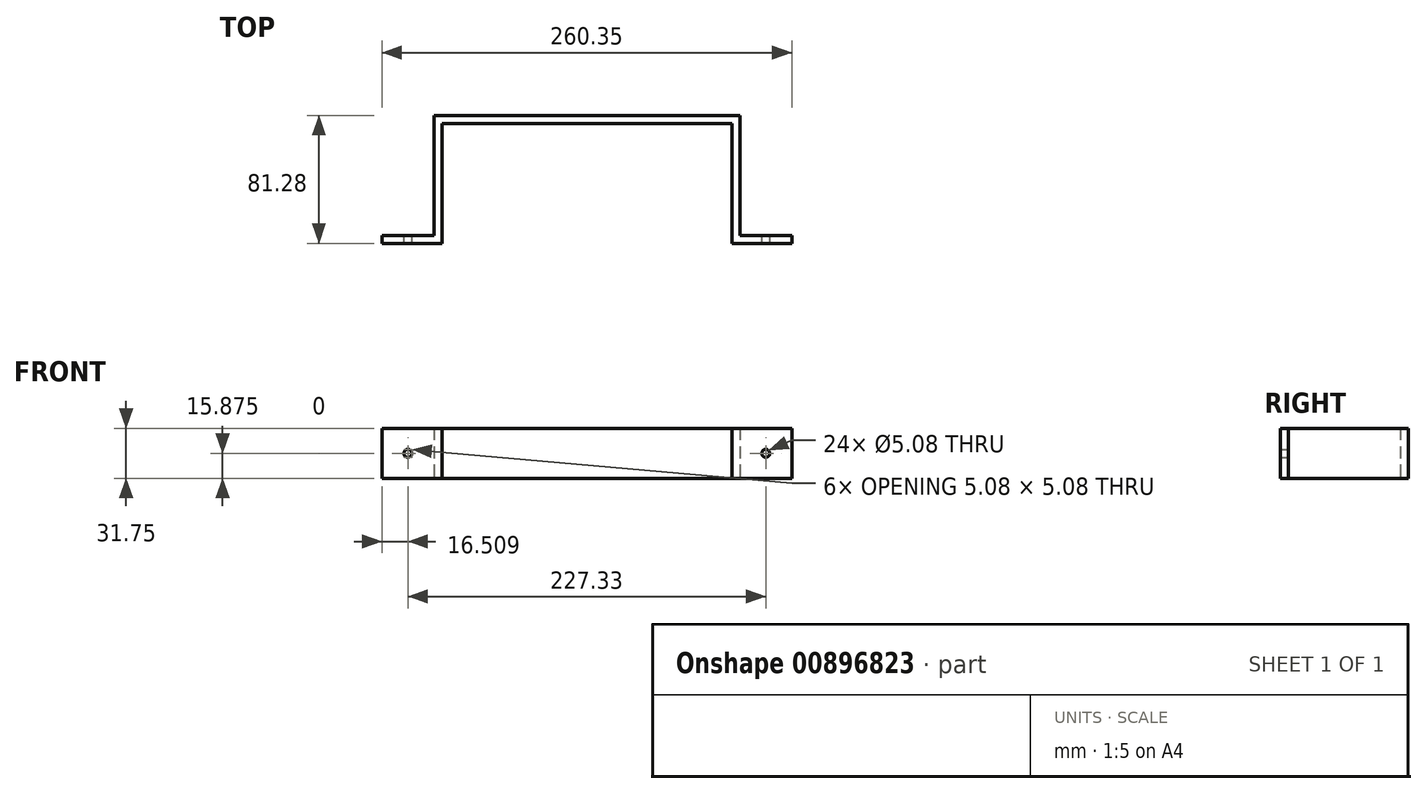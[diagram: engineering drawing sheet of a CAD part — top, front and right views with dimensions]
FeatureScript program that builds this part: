
annotation { "Feature Type Name" : "Feature", "Feature Type Description" : "" }
export const myFeature = defineFeature(function(context is Context, id is Id, definition is map)
    precondition{}
    {
        {
            var Q0;
            Q0=qCreatedBy(makeId("Top.planeOp"),FACE);
            var sketch = newSketch(context, id + "F0", { "sketchPlane" : qUnion([Q0])});
            skLineSegment(sketch, "E0", {"start": v(-81.06, 47.3) * mm, "end": v(103.09, 47.3) * mm});
            skLineSegment(sketch, "E1", {"start": v(103.09, 47.3) * mm, "end": v(103.09, -28.9) * mm});
            skLineSegment(sketch, "E2", {"start": v(-81.06, 47.3) * mm, "end": v(-81.06, -28.9) * mm});
            skLineSegment(sketch, "E3", {"start": v(-81.06, -28.9) * mm, "end": v(-119.16, -28.9) * mm});
            skLineSegment(sketch, "E4", {"start": v(103.09, -28.9) * mm, "end": v(141.19, -28.9) * mm});
            skLineSegment(sketch, "E5", {"start": v(-119.16, -28.9) * mm, "end": v(-119.16, -23.82) * mm});
            skLineSegment(sketch, "E6", {"start": v(-119.16, -23.82) * mm, "end": v(-86.14, -23.82) * mm});
            skLineSegment(sketch, "E7", {"start": v(-86.14, -23.82) * mm, "end": v(-86.14, 52.38) * mm});
            skLineSegment(sketch, "E8", {"start": v(-86.14, 52.38) * mm, "end": v(108.17, 52.38) * mm});
            skLineSegment(sketch, "E9", {"start": v(141.19, -28.9) * mm, "end": v(141.19, -23.82) * mm});
            skLineSegment(sketch, "E10", {"start": v(141.19, -23.82) * mm, "end": v(108.17, -23.82) * mm});
            skLineSegment(sketch, "E11", {"start": v(108.17, -23.82) * mm, "end": v(108.17, 52.38) * mm});
            skSolve(sketch);
        }
        {
            var Q0;
            Q0=makeQuery(id+"F0.imprint","IMPRINT",FACE,{"disambiguationData":[TD([[makeQuery(id+"F0.imprint","IMPRINT",EDGE,{"derivedFrom":sQuery(id+"F0.wireOp",EDGE,"E0")}),1.0]])]});
            extrude(context, id + "F1", {"entities" : qUnion([Q0]), "depth" : 31.75 * mm, "offsetDistance" : 25.4 * mm});
        }
        {
            var Q0;
            Q0=makeQuery(id+"F1.opExtrude","SWEPT_FACE",FACE,{"disambiguationData":[OSD([sQuery(id+"F0.wireOp",EDGE,"E6")])]});
            var sketch = newSketch(context, id + "F2", { "sketchPlane" : qUnion([Q0])});
            skCircle(sketch, "E12", {"center": v(102.65, 15.88) * mm, "radius": 3.18 * mm});
            skSolve(sketch);
        }
        {
            var Q0;
            Q0=sQuery(id+"F2.wireOp",VERTEX,"E12.center");
            var Q1;
            Q1=makeQuery(id+"F1.opExtrude","SWEPT_BODY",BODY,{"disambiguationData":[OSD([sQuery(id+"F0.wireOp",EDGE,"E0"),sQuery(id+"F0.wireOp",EDGE,"E1"),sQuery(id+"F0.wireOp",EDGE,"E2"),sQuery(id+"F0.wireOp",EDGE,"E3"),sQuery(id+"F0.wireOp",EDGE,"E4"),sQuery(id+"F0.wireOp",EDGE,"E5"),sQuery(id+"F0.wireOp",EDGE,"E6"),sQuery(id+"F0.wireOp",EDGE,"E7"),sQuery(id+"F0.wireOp",EDGE,"E8"),sQuery(id+"F0.wireOp",EDGE,"E9"),sQuery(id+"F0.wireOp",EDGE,"E10"),sQuery(id+"F0.wireOp",EDGE,"E11")])]});
            hole(context, id + "F3", {"style" : HoleStyle.SIMPLE, "endStyle" : HoleEndStyle.THROUGH, "holeDiameter" : 5.08 * mm, "majorDiameter" : 6.35 * mm, "isTappedThrough" : true, "tappedDepth" : 12.7 * mm, "tapClearance" : 3, "locations" : qUnion([Q0]), "scope" : qUnion([Q1])});
        }
        {
            var Q0;
            Q0=makeQuery(id+"F1.opExtrude","SWEPT_FACE",FACE,{"disambiguationData":[OSD([sQuery(id+"F0.wireOp",EDGE,"E10")])]});
            var sketch = newSketch(context, id + "F4", { "sketchPlane" : qUnion([Q0])});
            skCircle(sketch, "E13", {"center": v(-124.68, 15.88) * mm, "radius": 3.18 * mm});
            skSolve(sketch);
        }
        {
            var Q0;
            Q0=sQuery(id+"F4.wireOp",VERTEX,"E13.center");
            var Q1;
            Q1=makeQuery(id+"F1.opExtrude","SWEPT_BODY",BODY,{"disambiguationData":[OSD([sQuery(id+"F0.wireOp",EDGE,"E0"),sQuery(id+"F0.wireOp",EDGE,"E1"),sQuery(id+"F0.wireOp",EDGE,"E2"),sQuery(id+"F0.wireOp",EDGE,"E3"),sQuery(id+"F0.wireOp",EDGE,"E4"),sQuery(id+"F0.wireOp",EDGE,"E5"),sQuery(id+"F0.wireOp",EDGE,"E6"),sQuery(id+"F0.wireOp",EDGE,"E7"),sQuery(id+"F0.wireOp",EDGE,"E8"),sQuery(id+"F0.wireOp",EDGE,"E9"),sQuery(id+"F0.wireOp",EDGE,"E10"),sQuery(id+"F0.wireOp",EDGE,"E11")])]});
            hole(context, id + "F5", {"style" : HoleStyle.SIMPLE, "endStyle" : HoleEndStyle.THROUGH, "holeDiameter" : 5.08 * mm, "majorDiameter" : 6.35 * mm, "isTappedThrough" : true, "tappedDepth" : 12.7 * mm, "tapClearance" : 3, "locations" : qUnion([Q0]), "scope" : qUnion([Q1])});
        }
    });
